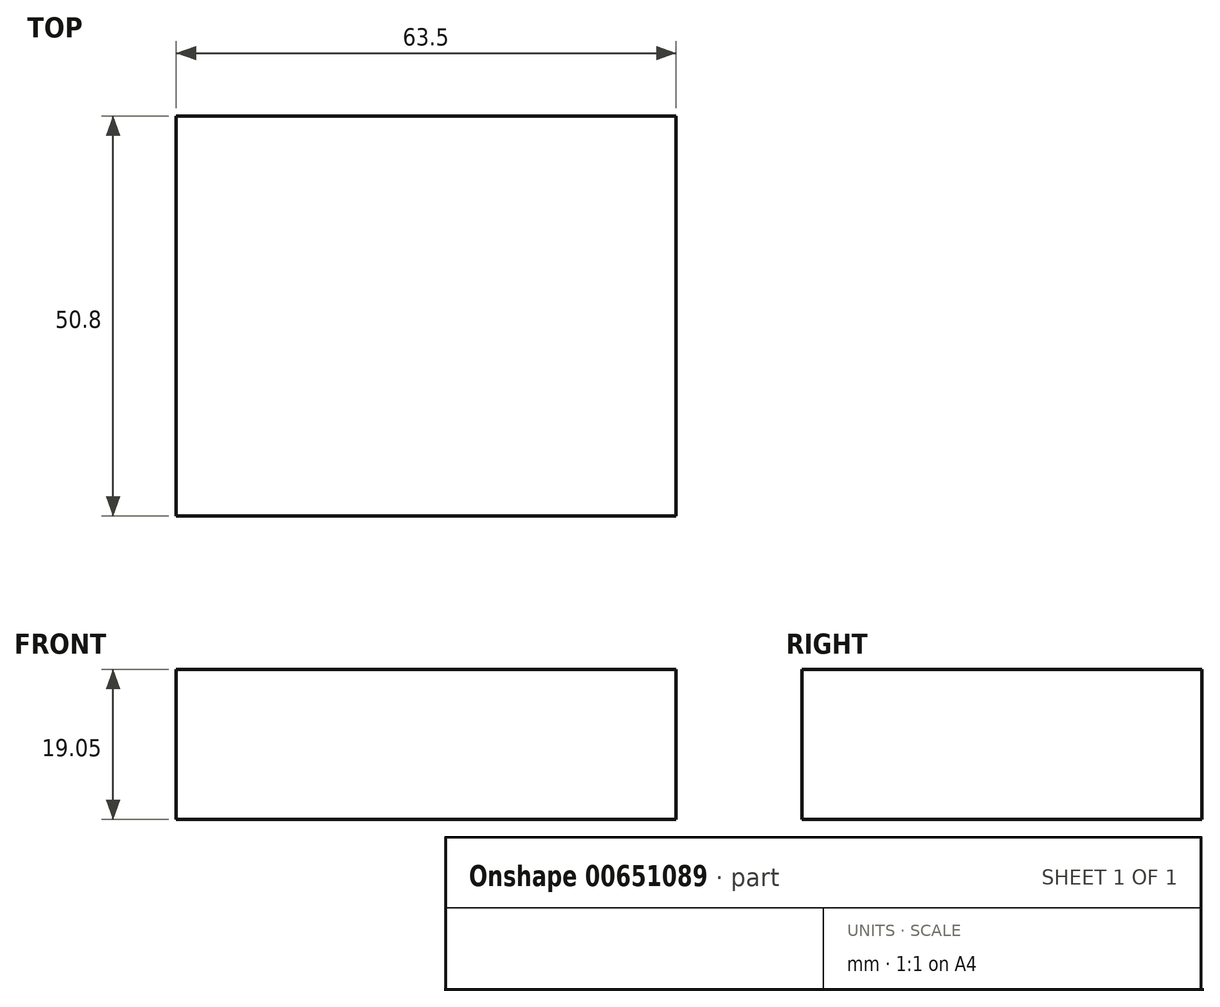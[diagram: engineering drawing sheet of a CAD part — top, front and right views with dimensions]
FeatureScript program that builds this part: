
annotation { "Feature Type Name" : "Feature", "Feature Type Description" : "" }
export const myFeature = defineFeature(function(context is Context, id is Id, definition is map)
    precondition{}
    {
        {
            var Q0;
            Q0=qCreatedBy(makeId("Top.planeOp"),FACE);
            var sketch = newSketch(context, id + "F0", { "sketchPlane" : qUnion([Q0])});
            skLineSegment(sketch, "E0", {"start": v(-22.7, 27.14) * mm, "end": v(-22.7, -23.66) * mm});
            skLineSegment(sketch, "E1", {"start": v(-22.7, -23.66) * mm, "end": v(40.8, -23.66) * mm});
            skLineSegment(sketch, "E2", {"start": v(40.8, -23.66) * mm, "end": v(40.8, 27.14) * mm});
            skLineSegment(sketch, "E3", {"start": v(40.8, 27.14) * mm, "end": v(-22.7, 27.14) * mm});
            skSolve(sketch);
        }
        {
            var Q0;
            Q0=makeQuery(id+"F0.imprint","IMPRINT",FACE,{"disambiguationData":[TD([[makeQuery(id+"F0.imprint","IMPRINT",EDGE,{"derivedFrom":sQuery(id+"F0.wireOp",EDGE,"E0")}),1.0]])]});
            extrude(context, id + "F1", {"entities" : qUnion([Q0]), "oppositeDirection" : true, "depth" : 19.05 * mm, "offsetDistance" : 25.4 * mm});
        }
    });
